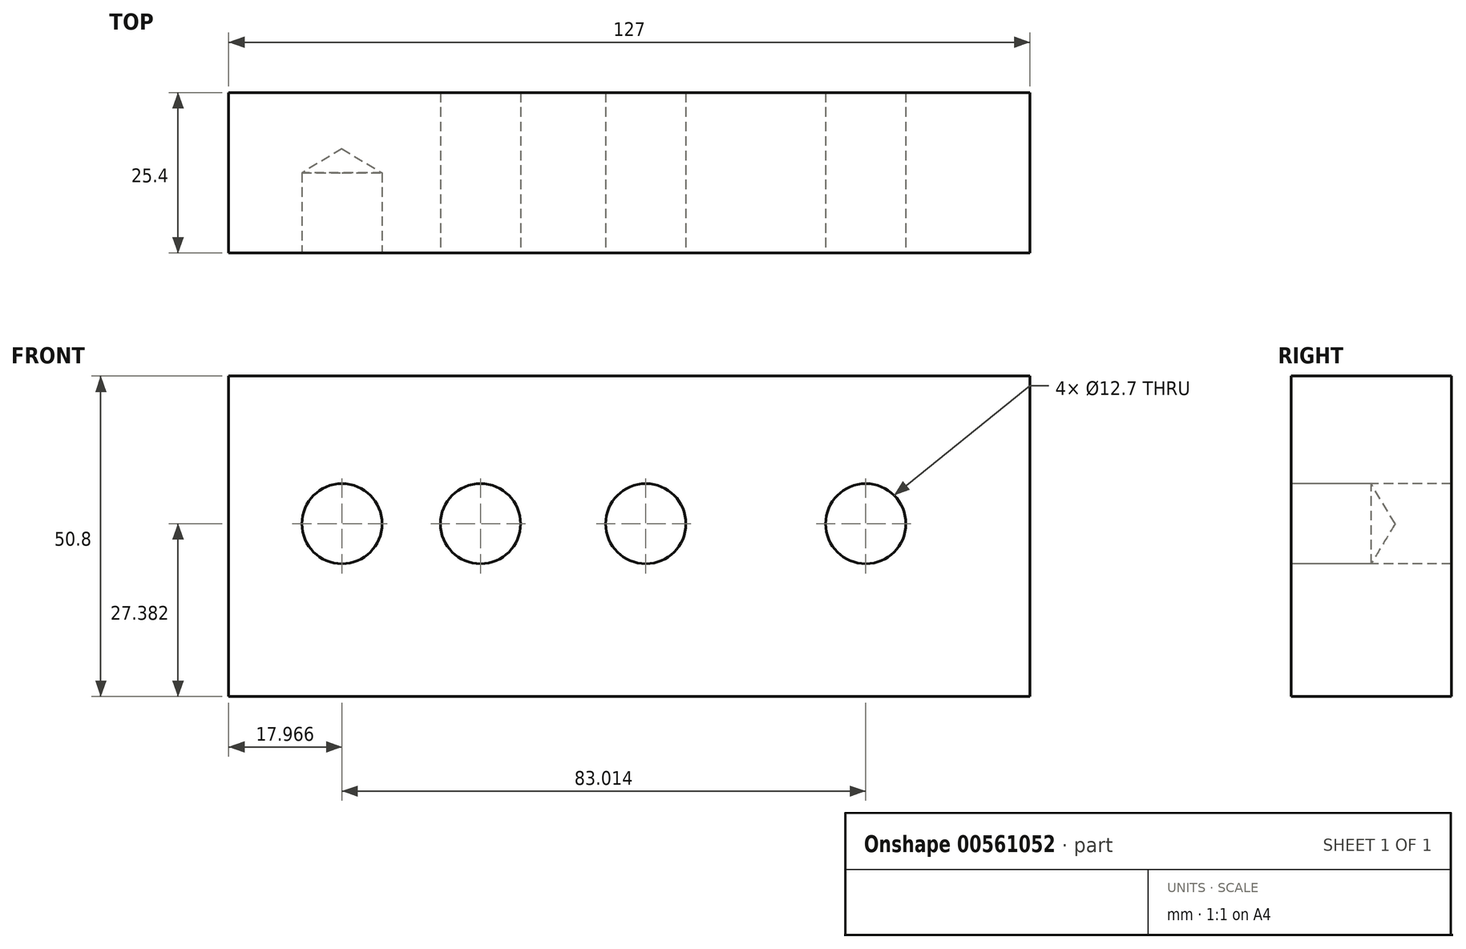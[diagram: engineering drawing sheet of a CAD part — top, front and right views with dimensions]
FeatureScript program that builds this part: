
annotation { "Feature Type Name" : "Feature", "Feature Type Description" : "" }
export const myFeature = defineFeature(function(context is Context, id is Id, definition is map)
    precondition{}
    {
        {
            var Q0;
            Q0=qCreatedBy(makeId("Front.planeOp"),FACE);
            var sketch = newSketch(context, id + "F0", { "sketchPlane" : qUnion([Q0])});
            skLineSegment(sketch, "E0", {"start": v(0, 0) * mm, "end": v(127, 0) * mm});
            skLineSegment(sketch, "E1", {"start": v(127, 0) * mm, "end": v(127, 50.8) * mm});
            skLineSegment(sketch, "E2", {"start": v(127, 50.8) * mm, "end": v(0, 50.8) * mm});
            skLineSegment(sketch, "E3", {"start": v(0, 50.8) * mm, "end": v(0, 0) * mm});
            skPoint(sketch, "E4", {"position": v(17.2, 25.84) * mm});
            skPoint(sketch, "E5", {"position": v(36.26, 25.84) * mm});
            skPoint(sketch, "E6", {"position": v(64.58, 25.84) * mm});
            skPoint(sketch, "E7", {"position": v(100.98, 25.84) * mm});
            skSolve(sketch);
        }
        {
            var Q0;
            Q0 = qSketchRegion(id + "F0", true);
            extrude(context, id + "F1", {"entities" : qUnion([Q0]), "depth" : 25.4 * mm, "offsetDistance" : 25.4 * mm});
        }
        {
            var Q0;
            Q0=makeQuery(id+"F1.opExtrude","CAP_FACE",FACE,{"disambiguationData":[OSD([sQuery(id+"F0.wireOp",EDGE,"E0"),sQuery(id+"F0.wireOp",EDGE,"E1"),sQuery(id+"F0.wireOp",EDGE,"E2"),sQuery(id+"F0.wireOp",EDGE,"E3")])],"isStart":false});
            var sketch = newSketch(context, id + "F2", { "sketchPlane" : qUnion([Q0])});
            skPoint(sketch, "E8", {"position": v(17.97, 27.38) * mm});
            skPoint(sketch, "E9", {"position": v(39.92, 27.38) * mm});
            skPoint(sketch, "E10", {"position": v(66.12, 27.38) * mm});
            skPoint(sketch, "E11", {"position": v(100.98, 27.38) * mm});
            skSolve(sketch);
        }
        {
            var Q0;
            Q0=sQuery(id+"F2.wireOp",VERTEX,"E8");
            var Q1;
            Q1=makeQuery(id+"F1.opExtrude","SWEPT_BODY",BODY,{"disambiguationData":[OSD([sQuery(id+"F0.wireOp",EDGE,"E0"),sQuery(id+"F0.wireOp",EDGE,"E1"),sQuery(id+"F0.wireOp",EDGE,"E2"),sQuery(id+"F0.wireOp",EDGE,"E3")])]});
            hole(context, id + "F3", {"style" : HoleStyle.C_BORE, "endStyle" : HoleEndStyle.BLIND, "holeDiameter" : 12.7 * mm, "cBoreDiameter" : 12.7 * mm, "cBoreDepth" : 6.35 * mm, "holeDepth" : 12.7 * mm, "isTappedThrough" : true, "tappedDepth" : 12.7 * mm, "tapClearance" : 3, "locations" : qUnion([Q0]), "scope" : qUnion([Q1])});
        }
        {
            var Q0;
            Q0=sQuery(id+"F2.wireOp",VERTEX,"E9");
            var Q1;
            Q1=makeQuery(id+"F1.opExtrude","SWEPT_BODY",BODY,{"disambiguationData":[OSD([sQuery(id+"F0.wireOp",EDGE,"E0"),sQuery(id+"F0.wireOp",EDGE,"E1"),sQuery(id+"F0.wireOp",EDGE,"E2"),sQuery(id+"F0.wireOp",EDGE,"E3")])]});
            hole(context, id + "F4", {"style" : HoleStyle.SIMPLE, "endStyle" : HoleEndStyle.THROUGH, "holeDiameter" : 12.7 * mm, "isTappedThrough" : true, "tappedDepth" : 12.7 * mm, "tapClearance" : 3, "locations" : qUnion([Q0]), "scope" : qUnion([Q1])});
        }
        {
            var Q0;
            Q0=sQuery(id+"F2.wireOp",VERTEX,"E10");
            var Q1;
            Q1=makeQuery(id+"F1.opExtrude","SWEPT_BODY",BODY,{"disambiguationData":[OSD([sQuery(id+"F0.wireOp",EDGE,"E0"),sQuery(id+"F0.wireOp",EDGE,"E1"),sQuery(id+"F0.wireOp",EDGE,"E2"),sQuery(id+"F0.wireOp",EDGE,"E3")])]});
            hole(context, id + "F5", {"style" : HoleStyle.SIMPLE, "endStyle" : HoleEndStyle.THROUGH, "holeDiameter" : 12.7 * mm, "isTappedThrough" : true, "tappedDepth" : 12.7 * mm, "tapClearance" : 3, "locations" : qUnion([Q0]), "scope" : qUnion([Q1])});
        }
        {
            var Q0;
            Q0=sQuery(id+"F2.wireOp",VERTEX,"E11");
            var Q1;
            Q1=makeQuery(id+"F1.opExtrude","SWEPT_BODY",BODY,{"disambiguationData":[OSD([sQuery(id+"F0.wireOp",EDGE,"E0"),sQuery(id+"F0.wireOp",EDGE,"E1"),sQuery(id+"F0.wireOp",EDGE,"E2"),sQuery(id+"F0.wireOp",EDGE,"E3")])]});
            hole(context, id + "F6", {"style" : HoleStyle.SIMPLE, "endStyle" : HoleEndStyle.THROUGH, "holeDiameter" : 12.7 * mm, "isTappedThrough" : true, "tappedDepth" : 12.7 * mm, "tapClearance" : 3, "locations" : qUnion([Q0]), "scope" : qUnion([Q1])});
        }
    });
